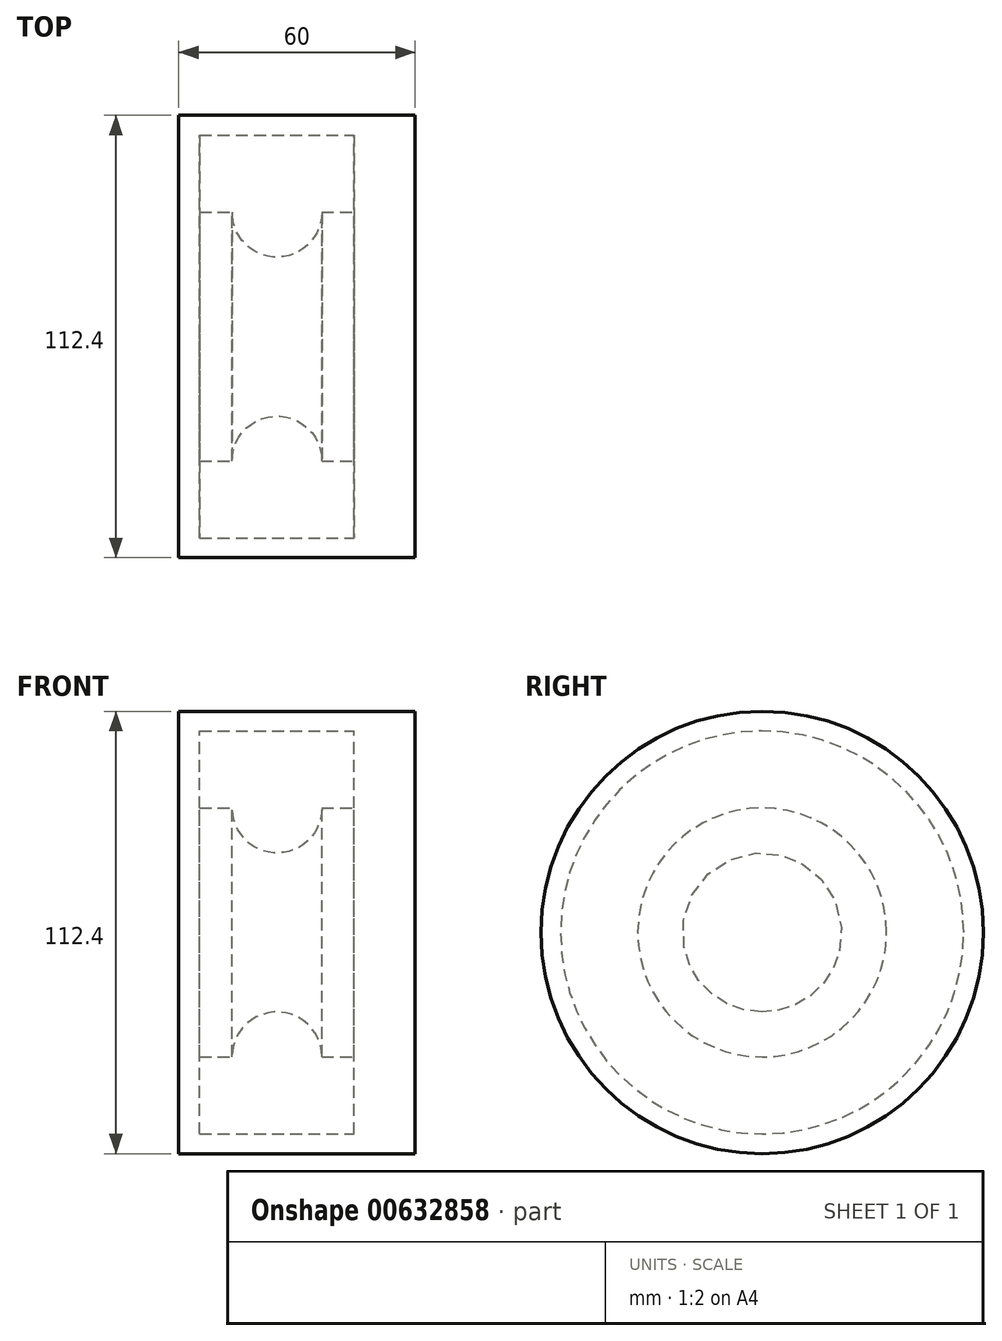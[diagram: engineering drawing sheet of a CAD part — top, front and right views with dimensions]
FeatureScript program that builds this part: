
annotation { "Feature Type Name" : "Feature", "Feature Type Description" : "" }
export const myFeature = defineFeature(function(context is Context, id is Id, definition is map)
    precondition{}
    {
        {
            var Q0;
            Q0=qCreatedBy(makeId("Front.planeOp"),FACE);
            var sketch = newSketch(context, id + "F0", { "sketchPlane" : qUnion([Q0])});
            skLineSegment(sketch, "E0.bottom", {"start": v(0, 0) * mm, "end": v(-60, 0) * mm});
            skLineSegment(sketch, "E0.top", {"start": v(0, 56.2) * mm, "end": v(-60, 56.2) * mm});
            skLineSegment(sketch, "E0.left", {"start": v(0, 0) * mm, "end": v(0, 56.2) * mm});
            skLineSegment(sketch, "E0.right", {"start": v(-60, 0) * mm, "end": v(-60, 56.2) * mm});
            skLineSegment(sketch, "E1.bottom", {"start": v(-54.7, 51.2) * mm, "end": v(-15.44, 51.2) * mm});
            skLineSegment(sketch, "E1.top", {"start": v(-54.7, 31.62) * mm, "end": v(-15.44, 31.62) * mm});
            skLineSegment(sketch, "E1.left", {"start": v(-54.7, 51.2) * mm, "end": v(-54.7, 31.62) * mm});
            skLineSegment(sketch, "E1.right", {"start": v(-15.44, 51.2) * mm, "end": v(-15.44, 31.62) * mm});
            skCircle(sketch, "E2", {"center": v(-35.07, 31.62) * mm, "radius": 11.41 * mm});
            skSolve(sketch);
        }
        {
            var Q0;
            Q0=makeQuery(id+"F0.imprint","IMPRINT",FACE,{"disambiguationData":[TD([[makeQuery(id+"F0.imprint","IMPRINT",EDGE,{"derivedFrom":sQuery(id+"F0.wireOp",EDGE,"E0.bottom")}),-1.0]])]});
            var Q1;
            Q1=sQuery(id+"F0.wireOp",EDGE,"E0.bottom");
            revolve(context, id + "F1", {"entities" : qUnion([Q0]), "axis" : qUnion([Q1]), "revolveType" : RevolveType.FULL});
        }
    });
